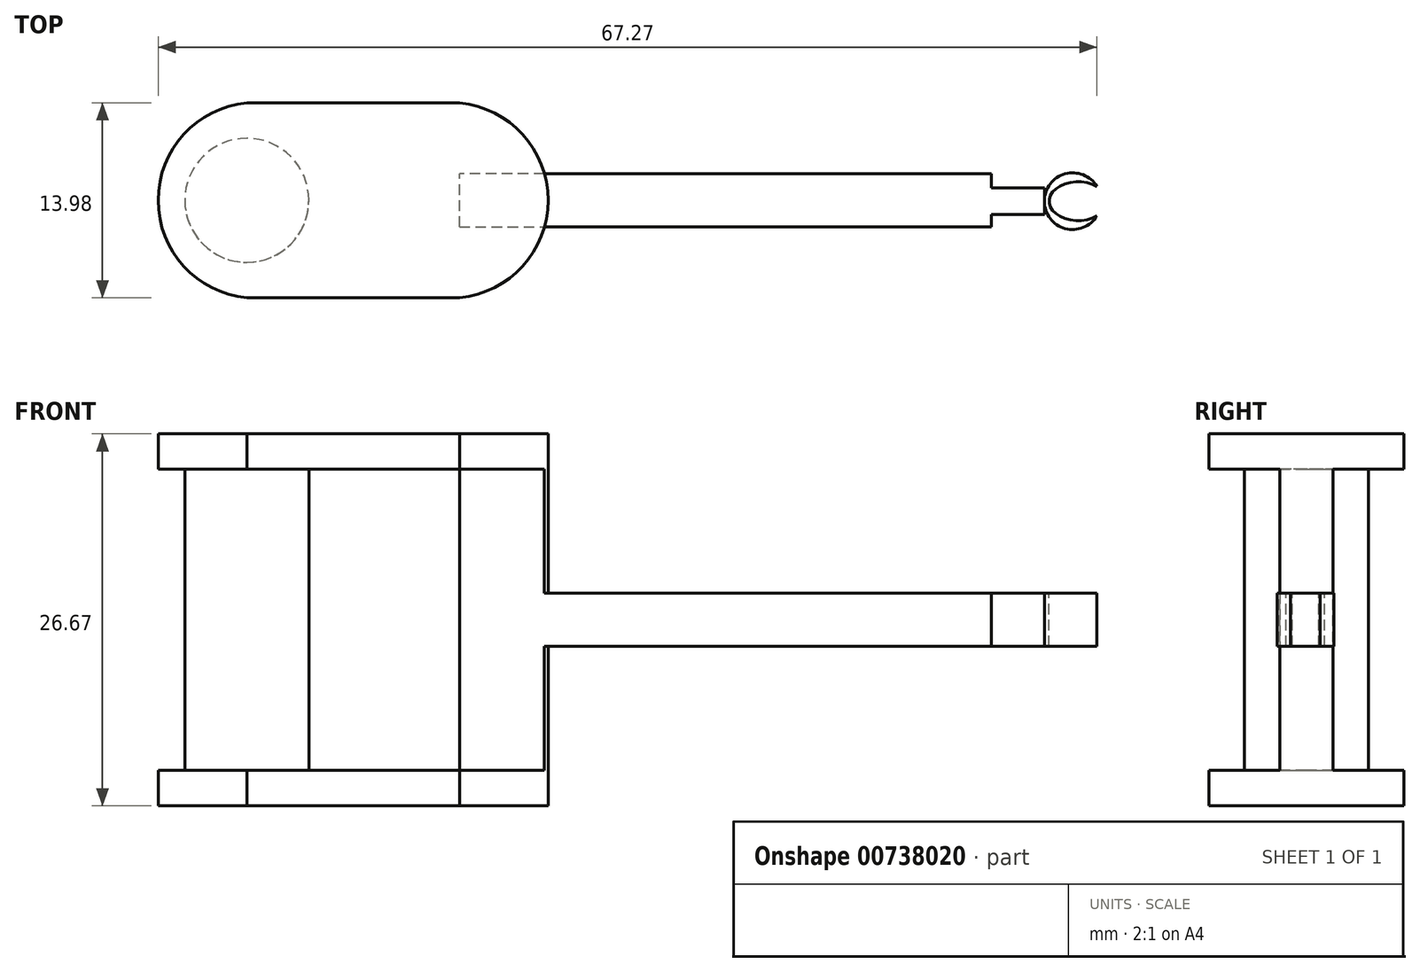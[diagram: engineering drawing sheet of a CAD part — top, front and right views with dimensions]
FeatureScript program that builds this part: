
annotation { "Feature Type Name" : "Feature", "Feature Type Description" : "" }
export const myFeature = defineFeature(function(context is Context, id is Id, definition is map)
    precondition{}
    {
        {
            var Q0;
            Q0=qCreatedBy(makeId("Front.planeOp"),FACE);
            var sketch = newSketch(context, id + "F0", { "sketchPlane" : qUnion([Q0])});
            skLineSegment(sketch, "E0", {"start": v(70.18, 20.45) * mm, "end": v(70.18, 16.64) * mm});
            skLineSegment(sketch, "E1", {"start": v(70.18, 16.64) * mm, "end": v(32.08, 16.64) * mm});
            skLineSegment(sketch, "E2", {"start": v(32.08, 16.64) * mm, "end": v(32.08, 20.45) * mm});
            skLineSegment(sketch, "E3", {"start": v(32.08, 20.45) * mm, "end": v(70.18, 20.45) * mm});
            skSolve(sketch);
        }
        {
            var Q0;
            Q0 = qSketchRegion(id + "F0", true);
            extrude(context, id + "F1", {"entities" : qUnion([Q0]), "endBound" : BoundingType.SYMMETRIC, "depth" : 3.8 * mm, "offsetDistance" : 25.4 * mm});
        }
        {
            var Q0;
            Q0=makeQuery(id+"F1.opExtrude","SWEPT_FACE",FACE,{"disambiguationData":[OSD([sQuery(id+"F0.wireOp",EDGE,"E3")])]});
            var sketch = newSketch(context, id + "F2", { "sketchPlane" : qUnion([Q0])});
            skLineSegment(sketch, "E4.0", {"start": v(32.08, -1.9) * mm, "end": v(32.08, 1.9) * mm});
            skArc(sketch, "E5", {"start": v(32.08, -6.99) * mm, "mid": v(38.43, 0) * mm, "end": v(32.08, 6.99) * mm});
            skLineSegment(sketch, "E6", {"start": v(32.08, 6.99) * mm, "end": v(16.84, 6.99) * mm});
            skLineSegment(sketch, "E7", {"start": v(32.08, -6.99) * mm, "end": v(16.84, -6.99) * mm});
            skArc(sketch, "E8", {"start": v(16.84, 6.99) * mm, "mid": v(10.49, 0) * mm, "end": v(16.84, -6.99) * mm});
            skLineSegment(sketch, "E9", {"start": v(16.84, 6.98) * mm, "end": v(16.84, -6.99) * mm, "construction": true});
            skSolve(sketch);
        }
        {
            var Q0;
            Q0 = qSketchRegion(id + "F2", true);
            extrude(context, id + "F3", {"entities" : qUnion([Q0]), "operationType" : NewBodyOperationType.ADD, "depth" : 11.43 * mm, "offsetDistance" : 25.4 * mm});
        }
        {
            var Q0;
            Q0=makeQuery(id+"F1.opExtrude","SWEPT_FACE",FACE,{"disambiguationData":[OSD([sQuery(id+"F0.wireOp",EDGE,"E1")])]});
            var sketch = newSketch(context, id + "F4", { "sketchPlane" : qUnion([Q0])});
            skArc(sketch, "E10.0", {"start": v(32.08, 6.99) * mm, "mid": v(38.43, 0) * mm, "end": v(32.08, -6.99) * mm});
            skLineSegment(sketch, "E10.1", {"start": v(32.08, 6.99) * mm, "end": v(16.84, 6.99) * mm});
            skLineSegment(sketch, "E10.2", {"start": v(32.08, -6.99) * mm, "end": v(16.84, -6.99) * mm});
            skArc(sketch, "E10.3", {"start": v(16.84, -6.99) * mm, "mid": v(10.49, 0) * mm, "end": v(16.84, 6.99) * mm});
            skSolve(sketch);
        }
        {
            var Q0;
            Q0 = qSketchRegion(id + "F4", true);
            extrude(context, id + "F5", {"entities" : qUnion([Q0]), "operationType" : NewBodyOperationType.ADD, "depth" : 11.43 * mm, "offsetDistance" : 25.4 * mm});
        }
        {
            var Q0;
            Q0=makeQuery(id+"F3.opExtrude","CAP_FACE",FACE,{"disambiguationData":[OSD([sQuery(id+"F2.wireOp",EDGE,"E5"),sQuery(id+"F2.wireOp",EDGE,"E6"),sQuery(id+"F2.wireOp",EDGE,"E7"),sQuery(id+"F2.wireOp",EDGE,"E8")])],"isStart":true});
            extrude(context, id + "F6", {"entities" : qUnion([Q0]), "operationType" : NewBodyOperationType.REMOVE, "oppositeDirection" : true, "depth" : 8.9 * mm, "offsetDistance" : 25.4 * mm});
        }
        {
            var Q0;
            Q0=makeQuery(id+"F5.opExtrude","CAP_FACE",FACE,{"disambiguationData":[OSD([sQuery(id+"F4.wireOp",EDGE,"E10.0"),sQuery(id+"F4.wireOp",EDGE,"E10.1"),sQuery(id+"F4.wireOp",EDGE,"E10.2"),sQuery(id+"F4.wireOp",EDGE,"E10.3")])],"isStart":true});
            extrude(context, id + "F7", {"entities" : qUnion([Q0]), "operationType" : NewBodyOperationType.REMOVE, "oppositeDirection" : true, "depth" : 8.9 * mm, "offsetDistance" : 25.4 * mm});
        }
        {
            var Q0;
            Q0=makeQuery(id+"F6.boolean.opBoolean","COPY",FACE,{"derivedFrom":makeQuery(id+"F6.opExtrude","CAP_FACE",FACE,{"disambiguationData":[OSD([sQuery(id+"F2.wireOp",EDGE,"E5"),sQuery(id+"F2.wireOp",EDGE,"E6"),sQuery(id+"F2.wireOp",EDGE,"E7"),sQuery(id+"F2.wireOp",EDGE,"E8")])],"isStart":false})});
            var sketch = newSketch(context, id + "F8", { "sketchPlane" : qUnion([Q0])});
            skLineSegment(sketch, "E11.0", {"start": v(16.84, -6.98) * mm, "end": v(16.84, 6.99) * mm, "construction": true});
            skCircle(sketch, "E12", {"center": v(16.84, 0) * mm, "radius": 4.45 * mm});
            skSolve(sketch);
        }
        {
            var Q0;
            Q0 = qSketchRegion(id + "F8", true);
            var Q1;
            Q1=sQuery(id+"F8.wireOp",EDGE,"E12");
            extrude(context, id + "F9", {"entities" : qUnion([Q0]), "operationType" : NewBodyOperationType.ADD, "surfaceEntities" : qUnion([Q1]), "endBound" : BoundingType.UP_TO_NEXT, "depth" : 25.4 * mm, "offsetDistance" : 25.4 * mm});
        }
        {
            var Q0;
            Q0=makeQuery(id+"F1.opExtrude","SWEPT_FACE",FACE,{"disambiguationData":[OSD([sQuery(id+"F0.wireOp",EDGE,"E3")])]});
            var sketch = newSketch(context, id + "F10", { "sketchPlane" : qUnion([Q0])});
            skLineSegment(sketch, "E13.0", {"start": v(70.18, -1.9) * mm, "end": v(70.18, 1.9) * mm});
            skLineSegment(sketch, "E14", {"start": v(70.18, 0.89) * mm, "end": v(73.99, 0.89) * mm});
            skLineSegment(sketch, "E15", {"start": v(73.99, 0.89) * mm, "end": v(73.99, -1.02) * mm});
            skLineSegment(sketch, "E16", {"start": v(73.99, -1.02) * mm, "end": v(70.18, -1.02) * mm});
            skLineSegment(sketch, "E17", {"start": v(70.18, -1.02) * mm, "end": v(70.18, 0.89) * mm});
            skLineSegment(sketch, "E18", {"start": v(73.99, -0.06) * mm, "end": v(76.02, -0.06) * mm, "construction": true});
            skCircle(sketch, "E19", {"center": v(76.02, -0.06) * mm, "radius": 2.03 * mm});
            skLineSegment(sketch, "E20", {"start": v(76.02, -0.06) * mm, "end": v(76.4, -0.06) * mm, "construction": true});
            skEllipse(sketch, "E21", {"center": v(76.4, -0.06) * mm, "majorRadius": 2.07 * mm, "minorRadius": 1.4 * mm, "majorAxis": v(-1, 0)});
            skSolve(sketch);
        }
        {
            var Q0;
            {var subQ3=sQuery(id+"F10.wireOp",EDGE,"E14");Q0=makeQuery(id+"F10.imprint","IMPRINT",FACE,{"disambiguationData":[TD([[makeQuery(id+"F10.imprint","IMPRINT",EDGE,{"derivedFrom":subQ3}),-1.0]])]});}
            var Q1;
            {var subQ0=sQuery(id+"F10.wireOp",EDGE,"E19");var subQ1=makeQuery(id+"F10.imprint","INTERSECT",VERTEX,{"derivedFrom":[sQuery(id+"F10.wireOp",EDGE,"E15"),subQ0]});Q1=makeQuery(id+"F10.imprint","IMPRINT",FACE,{"disambiguationData":[TD([[makeQuery(id+"F10.imprint","IMPRINT",EDGE,{"disambiguationData":[TD([[subQ1,1.0]])],"derivedFrom":subQ0}),1.0]])]});}
            extrude(context, id + "F11", {"entities" : qUnion([Q0, Q1]), "operationType" : NewBodyOperationType.ADD, "oppositeDirection" : true, "depth" : 3.8 * mm, "offsetDistance" : 25.4 * mm});
        }
    });
